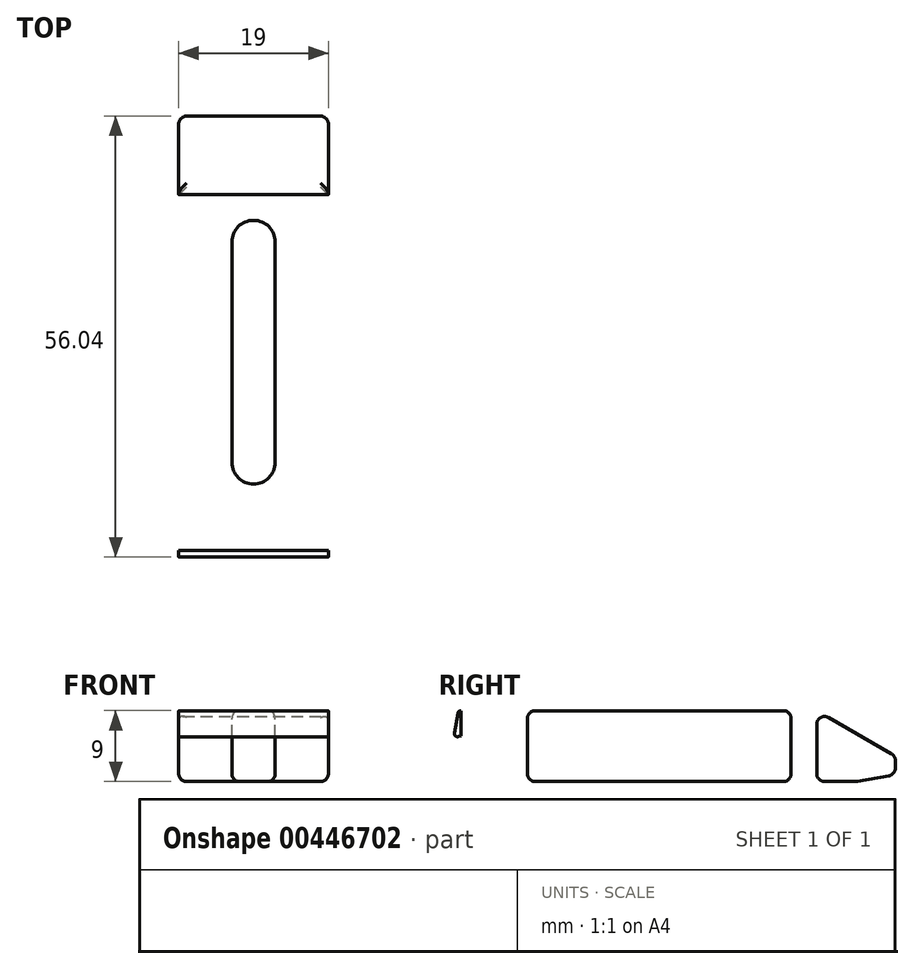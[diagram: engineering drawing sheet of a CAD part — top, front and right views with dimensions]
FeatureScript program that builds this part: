
annotation { "Feature Type Name" : "Feature", "Feature Type Description" : "" }
export const myFeature = defineFeature(function(context is Context, id is Id, definition is map)
    precondition{}
    {
        {
            var Q0;
            Q0=qCreatedBy(makeId("Right.planeOp"),FACE);
            var sketch = newSketch(context, id + "F0", { "sketchPlane" : qUnion([Q0])});
            skLineSegment(sketch, "E0", {"start": v(17.77, 4.07) * mm, "end": v(-27.43, 4.07) * mm});
            skLineSegment(sketch, "E1", {"start": v(-27.82, 3.74) * mm, "end": v(-28.27, 1.23) * mm});
            skLineSegment(sketch, "E2", {"start": v(-26.5, 1.14) * mm, "end": v(-27.76, 0.77) * mm});
            skLineSegment(sketch, "E3", {"start": v(17.77, 4.07) * mm, "end": v(27.77, -1.7) * mm});
            skLineSegment(sketch, "E4", {"start": v(27.77, -1.7) * mm, "end": v(27.77, -4.07) * mm});
            skLineSegment(sketch, "E5", {"start": v(27.77, -4.07) * mm, "end": v(22.84, -4.93) * mm});
            skLineSegment(sketch, "E6", {"start": v(22.84, -4.93) * mm, "end": v(-22.23, -4.93) * mm});
            skPoint(sketch, "E7.visualSharp", {"position": v(-27.77, 4.07) * mm});
            skArc(sketch, "E7.filletArc", {"start": v(-27.43, 4.07) * mm, "mid": v(-27.69, 3.97) * mm, "end": v(-27.82, 3.74) * mm});
            skPoint(sketch, "E8.visualSharp", {"position": v(-28.38, 0.6) * mm});
            skArc(sketch, "E8.filletArc", {"start": v(-28.27, 1.23) * mm, "mid": v(-28.14, 0.86) * mm, "end": v(-27.76, 0.77) * mm});
            skLineSegment(sketch, "E9", {"start": v(-25.99, 0.68) * mm, "end": v(-26.44, -1.9) * mm});
            skLineSegment(sketch, "E10", {"start": v(-25.94, -2.35) * mm, "end": v(-24.67, -1.99) * mm});
            skLineSegment(sketch, "E11", {"start": v(-24.17, -2.44) * mm, "end": v(-24.62, -5.02) * mm});
            skPoint(sketch, "E12.visualSharp", {"position": v(-25.88, 1.31) * mm});
            skArc(sketch, "E12.filletArc", {"start": v(-25.99, 0.68) * mm, "mid": v(-26.12, 1.05) * mm, "end": v(-26.5, 1.14) * mm});
            skPoint(sketch, "E13.visualSharp", {"position": v(-26.56, -2.53) * mm});
            skArc(sketch, "E13.filletArc", {"start": v(-26.44, -1.9) * mm, "mid": v(-26.32, -2.26) * mm, "end": v(-25.94, -2.35) * mm});
            skPoint(sketch, "E14.visualSharp", {"position": v(-24.06, -1.81) * mm});
            skArc(sketch, "E14.filletArc", {"start": v(-24.17, -2.44) * mm, "mid": v(-24.3, -2.07) * mm, "end": v(-24.67, -1.99) * mm});
            skLineSegment(sketch, "E15", {"start": v(-22.23, -4.93) * mm, "end": v(-24.12, -5.47) * mm});
            skPoint(sketch, "E16.visualSharp", {"position": v(-24.73, -5.65) * mm});
            skArc(sketch, "E16.filletArc", {"start": v(-24.62, -5.02) * mm, "mid": v(-24.5, -5.39) * mm, "end": v(-24.12, -5.47) * mm});
            skPoint(sketch, "E17", {"position": v(0, 0) * mm});
            skLineSegment(sketch, "E18", {"start": v(-27.77, 4.07) * mm, "end": v(27.77, -4.07) * mm, "construction": true});
            skLineSegment(sketch, "E19", {"start": v(0, 0) * mm, "end": v(24.8, 0) * mm, "construction": true});
            skSolve(sketch);
        }
        {
            var Q0;
            Q0=makeQuery(id+"F0.imprint","IMPRINT",FACE,{"disambiguationData":[TD([[makeQuery(id+"F0.imprint","IMPRINT",EDGE,{"derivedFrom":sQuery(id+"F0.wireOp",EDGE,"E0")}),1.0]])]});
            extrude(context, id + "F1", {"entities" : qUnion([Q0]), "depth" : 9.5 * mm, "hasSecondDirection" : true, "secondDirectionOppositeDirection" : true, "secondDirectionDepth" : 9.5 * mm});
        }
        {
            var Q0;
            Q0=makeQuery(id+"F1.opExtrude","SWEPT_FACE",FACE,{"disambiguationData":[OSD([sQuery(id+"F0.wireOp",EDGE,"E0")])]});
            var sketch = newSketch(context, id + "F2", { "sketchPlane" : qUnion([Q0])});
            skLineSegment(sketch, "E20", {"start": v(0, 17.77) * mm, "end": v(0, 11.77) * mm, "construction": true});
            skLineSegment(sketch, "E21", {"start": v(0, 11.77) * mm, "end": v(0, -16.23) * mm});
            skLineSegment(sketch, "E22", {"start": v(0, -16.23) * mm, "end": v(0, -22.23) * mm, "construction": true});
            skArc(sketch, "E23.0.startCap", {"start": v(-2.75, 11.77) * mm, "mid": v(0, 14.52) * mm, "end": v(2.75, 11.77) * mm});
            skArc(sketch, "E23.0.endCap", {"start": v(2.75, -16.23) * mm, "mid": v(0, -18.98) * mm, "end": v(-2.75, -16.23) * mm});
            skLineSegment(sketch, "E23.0.left", {"start": v(2.75, 11.77) * mm, "end": v(2.75, -16.23) * mm});
            skLineSegment(sketch, "E23.0.right", {"start": v(-2.75, 11.77) * mm, "end": v(-2.75, -16.23) * mm});
            skSolve(sketch);
        }
        {
            var Q0;
            Q0=makeQuery(id+"F2.imprint","IMPRINT",FACE,{"disambiguationData":[TD([[makeQuery(id+"F2.imprint","IMPRINT",EDGE,{"derivedFrom":sQuery(id+"F2.wireOp",EDGE,"E23.0.startCap")}),-1.0]])]});
            extrude(context, id + "F3", {"entities" : qUnion([Q0]), "operationType" : NewBodyOperationType.REMOVE, "endBound" : BoundingType.THROUGH_ALL, "oppositeDirection" : true, "depth" : 25 * mm});
        }
        {
            var Q0;
            Q0=makeQuery(id+"F1.opExtrude","SWEPT_FACE",FACE,{"disambiguationData":[OSD([sQuery(id+"F0.wireOp",EDGE,"E6")])]});
            var Q1;
            Q1=makeQuery(id+"F1.opExtrude","SWEPT_FACE",FACE,{"disambiguationData":[OSD([sQuery(id+"F0.wireOp",EDGE,"E0")])]});
            var Q2;
            Q2=makeQuery(id+"F1.opExtrude","SWEPT_FACE",FACE,{"disambiguationData":[OSD([sQuery(id+"F0.wireOp",EDGE,"E3")])]});
            var Q3;
            Q3=makeQuery(id+"F1.opExtrude","SWEPT_FACE",FACE,{"disambiguationData":[OSD([sQuery(id+"F0.wireOp",EDGE,"E4")])]});
            var Q4;
            Q4=makeQuery(id+"F1.opExtrude","SWEPT_FACE",FACE,{"disambiguationData":[OSD([sQuery(id+"F0.wireOp",EDGE,"E5")])]});
            fillet(context, id + "F4", {"entities" : qUnion([Q0, Q1, Q2, Q3, Q4]), "radius" : 1 * mm, "tangentPropagation" : true, "allowEdgeOverflow" : false});
        }
    });
